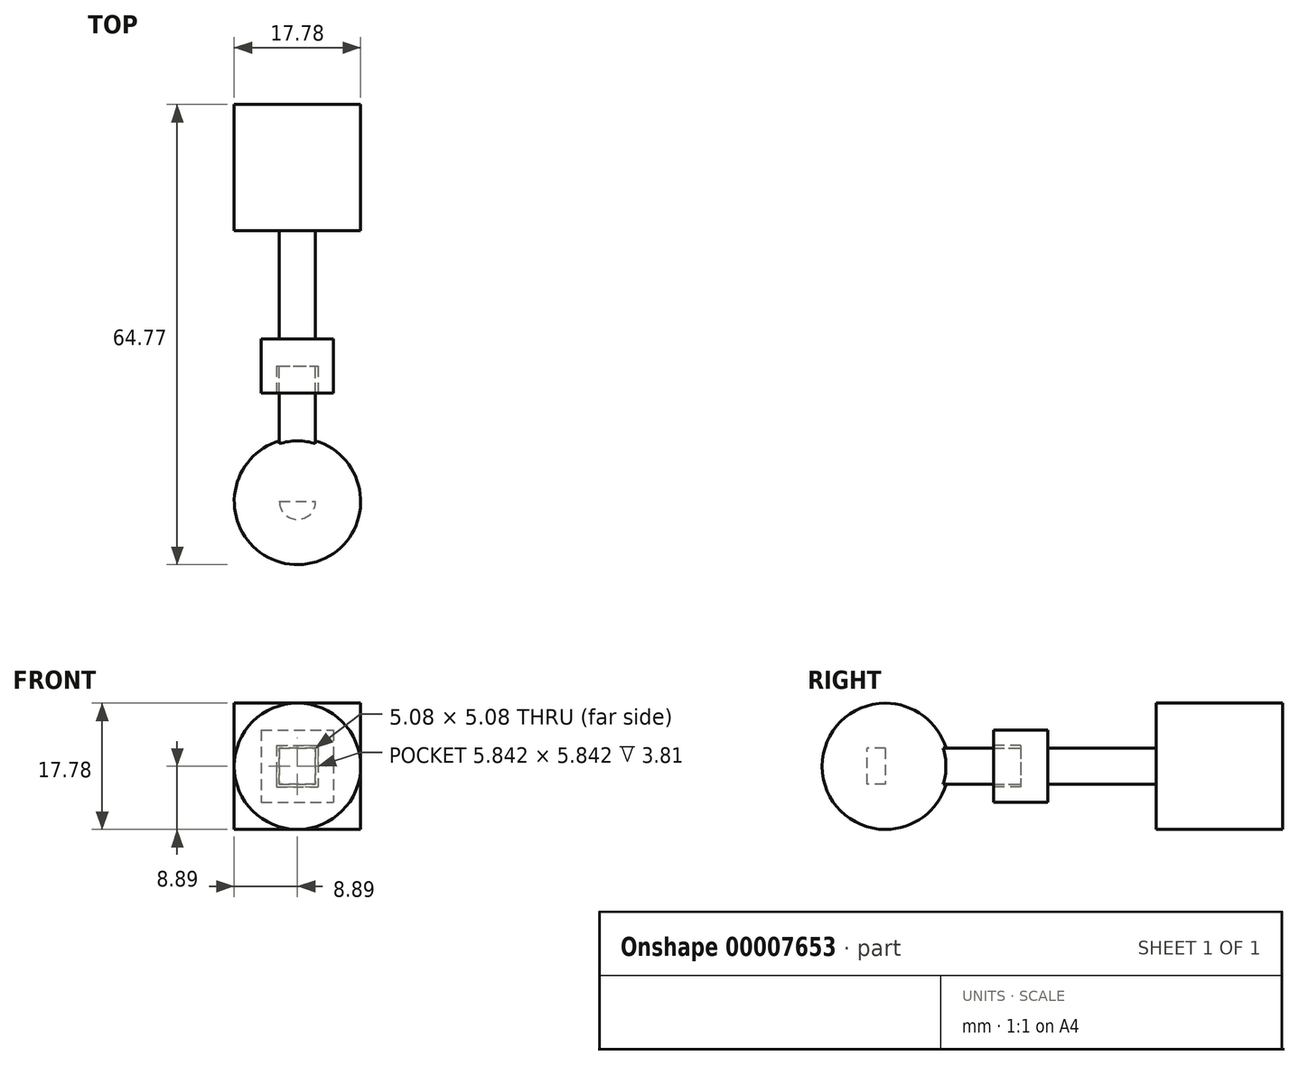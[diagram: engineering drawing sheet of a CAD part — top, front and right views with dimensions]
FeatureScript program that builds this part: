
annotation { "Feature Type Name" : "Feature", "Feature Type Description" : "" }
export const myFeature = defineFeature(function(context is Context, id is Id, definition is map)
    precondition{}
    {
        {
            var Q0;
            Q0=qCreatedBy(makeId("Front.planeOp"),FACE);
            var sketch = newSketch(context, id + "F0", { "sketchPlane" : qUnion([Q0])});
            skLineSegment(sketch, "E0.bottom", {"start": v(-8.9, 8.9) * mm, "end": v(8.89, 8.9) * mm});
            skLineSegment(sketch, "E0.top", {"start": v(-8.9, -8.9) * mm, "end": v(8.89, -8.9) * mm});
            skLineSegment(sketch, "E0.left", {"start": v(-8.89, 8.9) * mm, "end": v(-8.9, -8.9) * mm});
            skLineSegment(sketch, "E0.right", {"start": v(8.89, 8.9) * mm, "end": v(8.89, -8.9) * mm});
            skSolve(sketch);
        }
        {
            var Q0;
            Q0 = qSketchRegion(id + "F0", true);
            extrude(context, id + "F1", {"entities" : qUnion([Q0]), "depth" : 17.78 * mm});
        }
        {
            var Q0;
            Q0=makeQuery(id+"F1.opExtrude","CAP_FACE",FACE,{"disambiguationData":[OSD([sQuery(id+"F0.wireOp",EDGE,"E0.bottom"),sQuery(id+"F0.wireOp",EDGE,"E0.top"),sQuery(id+"F0.wireOp",EDGE,"E0.left"),sQuery(id+"F0.wireOp",EDGE,"E0.right")])],"isStart":false});
            var sketch = newSketch(context, id + "F2", { "sketchPlane" : qUnion([Q0])});
            skLineSegment(sketch, "E1.bottom", {"start": v(-2.54, 2.54) * mm, "end": v(2.54, 2.54) * mm});
            skLineSegment(sketch, "E1.top", {"start": v(-2.54, -2.54) * mm, "end": v(2.54, -2.54) * mm});
            skLineSegment(sketch, "E1.left", {"start": v(-2.54, 2.54) * mm, "end": v(-2.54, -2.54) * mm});
            skLineSegment(sketch, "E1.right", {"start": v(2.54, 2.54) * mm, "end": v(2.54, -2.54) * mm});
            skSolve(sketch);
        }
        {
            var Q0;
            Q0 = qSketchRegion(id + "F2", true);
            extrude(context, id + "F3", {"entities" : qUnion([Q0]), "operationType" : NewBodyOperationType.ADD, "depth" : 15.24 * mm});
        }
        {
            var Q0;
            Q0=makeQuery(id+"F3.opExtrude","CAP_FACE",FACE,{"disambiguationData":[OSD([sQuery(id+"F2.wireOp",EDGE,"E1.bottom"),sQuery(id+"F2.wireOp",EDGE,"E1.top"),sQuery(id+"F2.wireOp",EDGE,"E1.left"),sQuery(id+"F2.wireOp",EDGE,"E1.right")])],"isStart":false});
            var sketch = newSketch(context, id + "F4", { "sketchPlane" : qUnion([Q0])});
            skLineSegment(sketch, "E2.bottom", {"start": v(-5.08, 5.08) * mm, "end": v(5.08, 5.08) * mm});
            skLineSegment(sketch, "E2.top", {"start": v(-5.08, -5.08) * mm, "end": v(5.08, -5.08) * mm});
            skLineSegment(sketch, "E2.left", {"start": v(-5.08, 5.08) * mm, "end": v(-5.08, -5.08) * mm});
            skLineSegment(sketch, "E2.right", {"start": v(5.08, 5.08) * mm, "end": v(5.08, -5.08) * mm});
            skSolve(sketch);
        }
        {
            var Q0;
            Q0 = qSketchRegion(id + "F4", true);
            extrude(context, id + "F5", {"entities" : qUnion([Q0]), "operationType" : NewBodyOperationType.ADD, "depth" : 7.62 * mm});
        }
        {
            var Q0;
            Q0=makeQuery(id+"F5.opExtrude","CAP_FACE",FACE,{"disambiguationData":[OSD([sQuery(id+"F4.wireOp",EDGE,"E2.bottom"),sQuery(id+"F4.wireOp",EDGE,"E2.top"),sQuery(id+"F4.wireOp",EDGE,"E2.left"),sQuery(id+"F4.wireOp",EDGE,"E2.right")])],"isStart":false});
            var sketch = newSketch(context, id + "F6", { "sketchPlane" : qUnion([Q0])});
            skLineSegment(sketch, "E3.bottom", {"start": v(-2.92, 2.92) * mm, "end": v(2.92, 2.92) * mm});
            skLineSegment(sketch, "E3.top", {"start": v(-2.92, -2.92) * mm, "end": v(2.92, -2.92) * mm});
            skLineSegment(sketch, "E3.left", {"start": v(-2.92, 2.92) * mm, "end": v(-2.92, -2.92) * mm});
            skLineSegment(sketch, "E3.right", {"start": v(2.92, 2.92) * mm, "end": v(2.92, -2.92) * mm});
            skSolve(sketch);
        }
        {
            var Q0;
            Q0 = qSketchRegion(id + "F6", true);
            extrude(context, id + "F7", {"entities" : qUnion([Q0]), "operationType" : NewBodyOperationType.REMOVE, "oppositeDirection" : true, "depth" : 3.8 * mm});
        }
        {
            var Q0;
            Q0=makeQuery(id+"F7.boolean.opBoolean","COPY",FACE,{"derivedFrom":makeQuery(id+"F7.opExtrude","CAP_FACE",FACE,{"disambiguationData":[OSD([sQuery(id+"F6.wireOp",EDGE,"E3.bottom"),sQuery(id+"F6.wireOp",EDGE,"E3.top"),sQuery(id+"F6.wireOp",EDGE,"E3.left"),sQuery(id+"F6.wireOp",EDGE,"E3.right")])],"isStart":false})});
            var sketch = newSketch(context, id + "F8", { "sketchPlane" : qUnion([Q0])});
            skLineSegment(sketch, "E4.bottom", {"start": v(-2.54, 2.54) * mm, "end": v(2.54, 2.54) * mm});
            skLineSegment(sketch, "E4.top", {"start": v(-2.54, -2.54) * mm, "end": v(2.54, -2.54) * mm});
            skLineSegment(sketch, "E4.left", {"start": v(-2.54, 2.54) * mm, "end": v(-2.54, -2.54) * mm});
            skLineSegment(sketch, "E4.right", {"start": v(2.54, 2.54) * mm, "end": v(2.54, -2.54) * mm});
            skSolve(sketch);
        }
        {
            var Q0;
            Q0 = qSketchRegion(id + "F8", true);
            extrude(context, id + "F9", {"entities" : qUnion([Q0]), "depth" : 19.05 * mm});
        }
        {
            var Q0;
            Q0=makeQuery(id+"F9.opExtrude","CAP_FACE",FACE,{"disambiguationData":[OSD([sQuery(id+"F8.wireOp",EDGE,"E4.bottom"),sQuery(id+"F8.wireOp",EDGE,"E4.top"),sQuery(id+"F8.wireOp",EDGE,"E4.left"),sQuery(id+"F8.wireOp",EDGE,"E4.right")])],"isStart":false});
            var sketch = newSketch(context, id + "F10", { "sketchPlane" : qUnion([Q0])});
            skArc(sketch, "E5", {"start": v(0, -8.9) * mm, "mid": v(8.9, 0) * mm, "end": v(0, 8.9) * mm});
            skLineSegment(sketch, "E6", {"start": v(0, 8.9) * mm, "end": v(0, -8.9) * mm});
            skSolve(sketch);
        }
        {
            var Q0;
            {var subQ6=sQuery(id+"F10.wireOp",EDGE,"E5");Q0=makeQuery(id+"F10.imprint","IMPRINT",FACE,{"disambiguationData":[TD([[makeQuery(id+"F10.imprint","IMPRINT",EDGE,{"derivedFrom":subQ6}),1.0]])]});}
            var Q1;
            Q1=sQuery(id+"F10.wireOp",EDGE,"E6");
            revolve(context, id + "F11", {"operationType" : NewBodyOperationType.ADD, "entities" : qUnion([Q0]), "axis" : qUnion([Q1]), "revolveType" : RevolveType.FULL});
        }
    });
